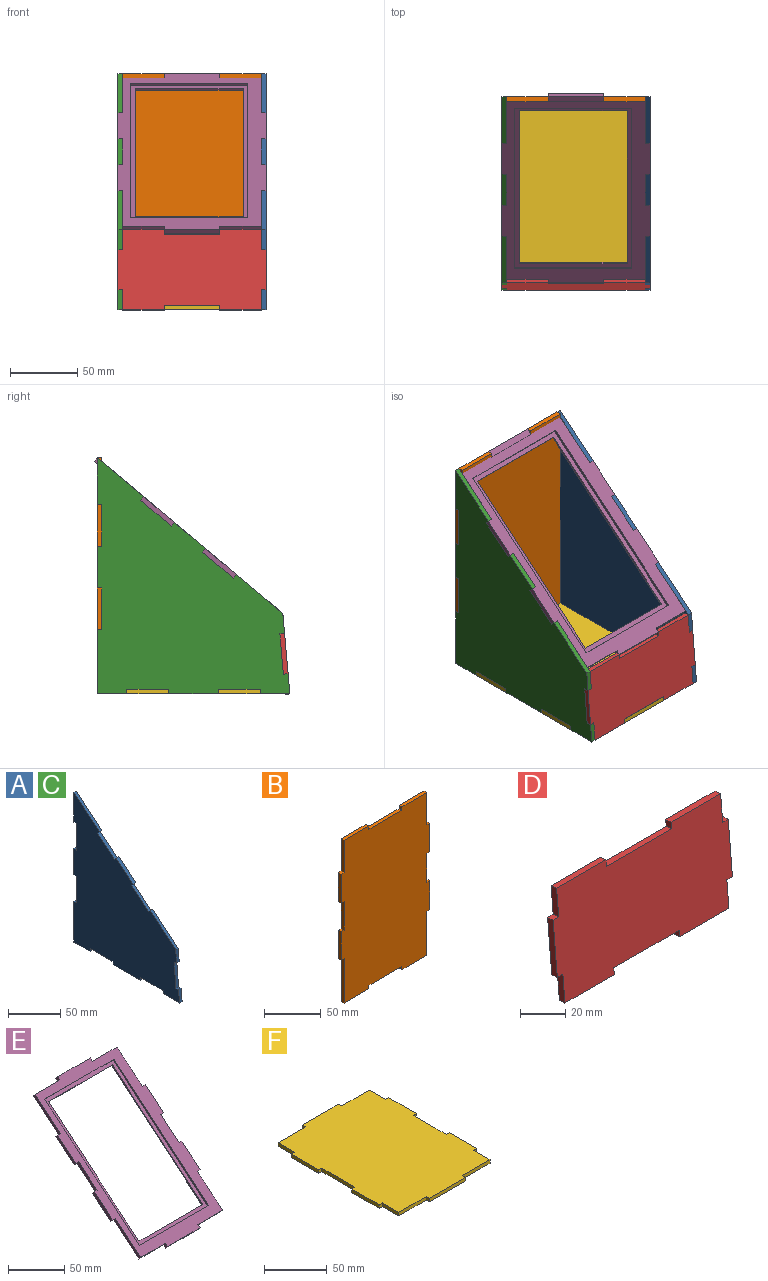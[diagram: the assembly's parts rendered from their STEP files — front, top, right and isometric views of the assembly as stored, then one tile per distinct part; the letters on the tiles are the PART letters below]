
ASSEMBLY  parts=6 mates=5
PART A: 34 faces, bbox 3.5x143.1x175.5 mm
  f0: plane 22.98x19.28mm, normal (0,-0.64,0.77), area 105mm2, adj f1,f31,f32,f33
  f1: plane 3.5x2.68mm, normal (0,0.77,0.64), area 12.2mm2, adj f0,f2,f32,f33
  f2: plane 34.47x28.93mm, normal (0,-0.64,0.77), area 157.5mm2, adj f1,f3,f32,f33
  f3: plane 14.94x3.5mm, normal (0,-1,0.09), area 52.5mm2, adj f2,f4,f32,f33
  f4: plane 3.5x3.49mm, normal (0,-0.09,-1), area 12.2mm2, adj f3,f5,f32,f33
  f5: plane 29.89x3.5mm, normal (0,-1,0.09), area 105mm2, adj f4,f6,f32,f33
  f6: plane 3.5x3.49mm, normal (0,0.09,1), area 12.3mm2, adj f5,f7,f32,f33
  f7: plane 14.94x3.5mm, normal (0,-1,0.09), area 52.5mm2, adj f6,f8,f32,f33
  f8: plane 22x3.5mm, normal (0,0,-1), area 77mm2, adj f7,f9,f32,f33
  f9: plane 3.5x3.5mm, normal (0,1,0), area 12.2mm2, adj f8,f10,f32,f33
  f10: plane 31x3.5mm, normal (0,0,-1), area 108.5mm2, adj f9,f11,f32,f33
  f11: plane 3.5x3.5mm, normal (0,-1,0), area 12.2mm2, adj f10,f12,f32,f33
  f12: plane 37.12x3.5mm, normal (0,0,-1), area 129.9mm2, adj f11,f13,f32,f33
  f13: plane 3.5x3.5mm, normal (0,1,0), area 12.2mm2, adj f12,f14,f32,f33
  f14: plane 31x3.5mm, normal (0,0,-1), area 108.5mm2, adj f13,f15,f32,f33
  f15: plane 3.5x3.5mm, normal (0,-1,0), area 12.2mm2, adj f14,f16,f32,f33
  f16: plane 22x3.5mm, normal (0,0,-1), area 77mm2, adj f15,f17,f32,f33
  f17: plane 47.67x3.5mm, normal (0,1,0), area 166.9mm2, adj f16,f18,f32,f33
  f18: plane 3.5x3.5mm, normal (0,0,1), area 12.3mm2, adj f17,f19,f32,f33
  f19: plane 31x3.5mm, normal (0,1,0), area 108.5mm2, adj f18,f20,f32,f33
  f20: plane 3.5x3.5mm, normal (0,0,-1), area 12.3mm2, adj f19,f21,f32,f33
  f21: plane 31x3.5mm, normal (0,1,0), area 108.5mm2, adj f20,f22,f32,f33
  f22: plane 3.5x3.5mm, normal (0,0,1), area 12.3mm2, adj f21,f23,f32,f33
  f23: plane 31x3.5mm, normal (0,1,0), area 108.5mm2, adj f22,f24,f32,f33
  f24: plane 3.5x3.5mm, normal (0,0,-1), area 12.3mm2, adj f23,f25,f32,f33
  f25: plane 34.8x3.5mm, normal (0,1,0), area 121.8mm2, adj f24,f26,f32,f33
  f26: plane 34.47x28.93mm, normal (0,-0.64,0.77), area 157.5mm2, adj f25,f27,f32,f33
  f27: plane 3.5x2.68mm, normal (0,-0.77,-0.64), area 12.2mm2, adj f26,f28,f32,f33
  f28: plane 22.98x19.28mm, normal (0,-0.64,0.77), area 105mm2, adj f27,f29,f32,f33
  f29: plane 3.5x2.68mm, normal (0,0.77,0.64), area 12.3mm2, adj f28,f30,f32,f33
  f30: plane 22.98x19.28mm, normal (0,-0.64,0.77), area 105mm2, adj f29,f31,f32,f33
  f31: plane 3.5x2.68mm, normal (0,-0.77,-0.64), area 12.3mm2, adj f0,f30,f32,f33
  f32: plane 175.47x143.12mm, normal (1,0,0), area 15626mm2, adj f0,f1,f2,f3,f4,f5,f6,f7
  f33: plane 175.47x143.12mm, normal (-1,0,0), area 15626mm2, adj f0,f1,f2,f3,f4,f5,f6,f7
PART B: 30 faces, bbox 110x3.5x175.5 mm
  f0: plane 3.5x3.5mm, normal (0,0,1), area 12.3mm2, adj f1,f27,f28,f29
  f1: plane 31x3.5mm, normal (1,0,0), area 108.5mm2, adj f0,f2,f28,f29
  f2: plane 3.5x3.5mm, normal (0,0,-1), area 12.3mm2, adj f1,f3,f28,f29
  f3: plane 31x3.5mm, normal (1,0,0), area 108.5mm2, adj f2,f4,f28,f29
  f4: plane 3.5x3.5mm, normal (0,0,1), area 12.3mm2, adj f3,f5,f28,f29
  f5: plane 31x3.5mm, normal (1,0,0), area 108.5mm2, adj f4,f6,f28,f29
  f6: plane 3.5x3.5mm, normal (0,0,-1), area 12.3mm2, adj f5,f7,f28,f29
  f7: plane 47.67x3.5mm, normal (1,0,0), area 166.9mm2, adj f6,f8,f28,f29
  f8: plane 31x3.5mm, normal (0,0,-1), area 108.5mm2, adj f7,f9,f28,f29
  f9: plane 3.5x3.5mm, normal (-1,0,0), area 12.2mm2, adj f8,f10,f28,f29
  f10: plane 41x3.5mm, normal (0,0,-1), area 143.5mm2, adj f9,f11,f28,f29
  f11: plane 3.5x3.5mm, normal (1,0,0), area 12.2mm2, adj f10,f12,f28,f29
  f12: plane 31x3.5mm, normal (0,0,-1), area 108.5mm2, adj f11,f13,f28,f29
  f13: plane 47.67x3.5mm, normal (-1,0,0), area 166.9mm2, adj f12,f14,f28,f29
  f14: plane 3.5x3.5mm, normal (0,0,-1), area 12.3mm2, adj f13,f15,f28,f29
  f15: plane 31x3.5mm, normal (-1,0,0), area 108.5mm2, adj f14,f16,f28,f29
  f16: plane 3.5x3.5mm, normal (0,0,1), area 12.3mm2, adj f15,f17,f28,f29
  f17: plane 31x3.5mm, normal (-1,0,0), area 108.5mm2, adj f16,f18,f28,f29
  f18: plane 3.5x3.5mm, normal (0,0,-1), area 12.3mm2, adj f17,f19,f28,f29
  f19: plane 31x3.5mm, normal (-1,0,0), area 108.5mm2, adj f18,f20,f28,f29
  f20: plane 3.5x3.5mm, normal (0,0,1), area 12.3mm2, adj f19,f21,f28,f29
  f21: plane 34.8x3.5mm, normal (-1,0,0), area 121.8mm2, adj f20,f22,f28,f29
  f22: plane 31x3.5mm, normal (0,0,1), area 108.5mm2, adj f21,f23,f28,f29
  f23: plane 3.5x3.5mm, normal (1,0,0), area 12.3mm2, adj f22,f24,f28,f29
  f24: plane 41x3.5mm, normal (0,0,1), area 143.5mm2, adj f23,f25,f28,f29
  f25: plane 3.5x3.5mm, normal (-1,0,0), area 12.3mm2, adj f24,f26,f28,f29
  f26: plane 31x3.5mm, normal (0,0,1), area 108.5mm2, adj f25,f27,f28,f29
  f27: plane 34.8x3.5mm, normal (1,0,0), area 121.8mm2, adj f0,f26,f28,f29
  f28: plane 175.47x110mm, normal (0,1,0), area 18220.8mm2, adj f0,f1,f2,f3,f4,f5,f6,f7
  f29: plane 175.47x110mm, normal (0,-1,0), area 18220.8mm2, adj f0,f1,f2,f3,f4,f5,f6,f7
PART C: same geometry as A
PART D: 27 faces, bbox 110x8.7x60.1 mm
  f0: plane 110x59.77mm, normal (0,1,-0.09), area 4303mm2, adj f1,f2,f3,f4,f5,f6,f7,f8
  f1: plane 15.25x4.79mm, normal (1,0,0), area 52.5mm2, adj f0,f2,f20,f21
  f2: plane 31x3.49mm, normal (0,0.09,1), area 108.5mm2, adj f0,f1,f3,f21
  f3: plane 3.79x3.79mm, normal (-1,0,0), area 12.3mm2, adj f0,f2,f4,f21
  f4: plane 41x3.49mm, normal (0,0.09,1), area 143.5mm2, adj f0,f3,f5,f21
  f5: plane 3.79x3.79mm, normal (1,0,0), area 12.3mm2, adj f0,f4,f6,f21
  f6: plane 31x3.49mm, normal (0,0.09,1), area 108.5mm2, adj f0,f5,f7,f21
  f7: plane 15.25x4.79mm, normal (-1,0,0), area 52.5mm2, adj f0,f6,f8,f21
  f8: plane 3.5x3.49mm, normal (0,0.09,1), area 12.3mm2, adj f0,f7,f9,f21
  f9: plane 30.19x6.1mm, normal (-1,0,0), area 105mm2, adj f0,f8,f10,f21
  f10: plane 3.5x3.49mm, normal (0,-0.09,-1), area 12.2mm2, adj f0,f9,f11,f21
  f11: plane 15.25x4.79mm, normal (-1,0,0), area 52.5mm2, adj f0,f10,f12,f21
  f12: plane 31x3.49mm, normal (0,-0.09,-1), area 108.5mm2, adj f0,f11,f13,f21
  f13: plane 3.79x3.79mm, normal (1,0,0), area 12.3mm2, adj f0,f12,f14,f21
  f14: plane 41x3.49mm, normal (0,-0.09,-1), area 143.5mm2, adj f0,f13,f15,f21
  f15: plane 3.79x3.79mm, normal (-1,0,0), area 12.3mm2, adj f0,f14,f16,f21
  f16: plane 31x3.49mm, normal (0,-0.09,-1), area 108.5mm2, adj f0,f15,f17,f21
  f17: plane 15.25x4.79mm, normal (1,0,0), area 52.5mm2, adj f0,f16,f18,f21
  f18: plane 3.5x3.49mm, normal (0,-0.09,-1), area 12.2mm2, adj f0,f17,f19,f21
  f19: plane 30.19x6.1mm, normal (1,0,0), area 105mm2, adj f0,f18,f20,f21
  f20: plane 3.5x3.49mm, normal (0,0.09,1), area 12.3mm2, adj f0,f1,f19,f21
  f21: plane 110x59.77mm, normal (0,-1,0.09), area 6103mm2, adj f1,f2,f3,f4,f5,f6,f7,f8
  f22: plane 45x2.49mm, normal (0,-0.09,-1), area 112.5mm2, adj f0,f23,f25,f26
  f23: plane 40.07x5.98mm, normal (-1,0,0), area 100mm2, adj f0,f22,f24,f26
  f24: plane 45x2.49mm, normal (0,0.09,1), area 112.5mm2, adj f0,f23,f25,f26
  f25: plane 40.07x5.98mm, normal (1,0,0), area 100mm2, adj f0,f22,f24,f26
  f26: plane 45x39.85mm, normal (0,1,-0.09), area 1800mm2, adj f22,f23,f24,f25
PART E: 39 faces, bbox 110x140.1x118.4 mm
  f0: plane 120.02x101.16mm, normal (1,0,0), area 310mm2, adj f1,f31,f32,f38
  f1: plane 87x1.53mm, normal (0,-0.77,-0.64), area 174mm2, adj f0,f2,f32,f38
  f2: plane 120.02x101.16mm, normal (-1,0,0), area 310mm2, adj f1,f31,f32,f38
  f3: plane 31x2.68mm, normal (0,0.77,0.64), area 108.5mm2, adj f4,f30,f32,f33
  f4: plane 4.93x4.93mm, normal (1,0,0), area 12.3mm2, adj f3,f5,f32,f33
  f5: plane 41x2.68mm, normal (0,0.77,0.64), area 143.5mm2, adj f4,f6,f32,f33
  f6: plane 4.93x4.93mm, normal (-1,0,0), area 12.2mm2, adj f5,f7,f32,f33
  f7: plane 31x2.68mm, normal (0,0.77,0.64), area 108.5mm2, adj f6,f8,f32,f33
  f8: plane 34.04x29.36mm, normal (-1,0,0), area 145.3mm2, adj f7,f9,f32,f33
  f9: plane 3.5x2.68mm, normal (0,0.77,0.64), area 12.3mm2, adj f8,f10,f32,f33
  f10: plane 25.23x21.96mm, normal (-1,0,0), area 105mm2, adj f9,f11,f32,f33
  f11: plane 3.5x2.68mm, normal (0,-0.77,-0.64), area 12.2mm2, adj f10,f12,f32,f33
  f12: plane 25.23x21.96mm, normal (-1,0,0), area 105mm2, adj f11,f13,f32,f33
  f13: plane 3.5x2.68mm, normal (0,0.77,0.64), area 12.2mm2, adj f12,f14,f32,f33
  f14: plane 25.23x21.96mm, normal (-1,0,0), area 105mm2, adj f13,f15,f32,f33
  f15: plane 3.5x2.68mm, normal (0,-0.77,-0.64), area 12.3mm2, adj f14,f16,f32,f33
  f16: plane 34.04x29.36mm, normal (-1,0,0), area 145.3mm2, adj f15,f17,f32,f33
  f17: plane 31x2.68mm, normal (0,-0.77,-0.64), area 108.5mm2, adj f16,f18,f32,f33
  f18: plane 4.93x4.93mm, normal (-1,0,0), area 12.3mm2, adj f17,f19,f32,f33
  f19: plane 41x2.68mm, normal (0,-0.77,-0.64), area 143.5mm2, adj f18,f20,f32,f33
  f20: plane 4.93x4.93mm, normal (1,0,0), area 12.3mm2, adj f19,f21,f32,f33
  f21: plane 31x2.68mm, normal (0,-0.77,-0.64), area 108.5mm2, adj f20,f22,f32,f33
  f22: plane 34.04x29.36mm, normal (1,0,0), area 145.3mm2, adj f21,f23,f32,f33
  f23: plane 3.5x2.68mm, normal (0,-0.77,-0.64), area 12.3mm2, adj f22,f24,f32,f33
  f24: plane 25.23x21.96mm, normal (1,0,0), area 105mm2, adj f23,f25,f32,f33
  f25: plane 3.5x2.68mm, normal (0,0.77,0.64), area 12.2mm2, adj f24,f26,f32,f33
  f26: plane 25.23x21.96mm, normal (1,0,0), area 105mm2, adj f25,f27,f32,f33
  f27: plane 3.5x2.68mm, normal (0,-0.77,-0.64), area 12.2mm2, adj f26,f28,f32,f33
  f28: plane 25.23x21.96mm, normal (1,0,0), area 105mm2, adj f27,f29,f32,f33
  f29: plane 3.5x2.68mm, normal (0,0.77,0.64), area 12.3mm2, adj f28,f30,f32,f33
  f30: plane 34.04x29.36mm, normal (1,0,0), area 145.3mm2, adj f3,f29,f32,f33
  f31: plane 87x1.53mm, normal (0,0.77,0.64), area 174mm2, adj f0,f2,f32,f38
  f32: plane 137.89x115.7mm, normal (0,-0.64,0.77), area 5041mm2, adj f0,f1,f2,f3,f4,f5,f6,f7
  f33: plane 137.89x115.7mm, normal (0,0.64,-0.77), area 6686mm2, adj f3,f4,f5,f6,f7,f8,f9,f10
  f34: plane 114.34x96.28mm, normal (1,0,0), area 222mm2, adj f33,f35,f37,f38
  f35: plane 80x1.15mm, normal (0,-0.77,-0.64), area 120mm2, adj f33,f34,f36,f38
  f36: plane 114.34x96.28mm, normal (-1,0,0), area 222mm2, adj f33,f35,f37,f38
  f37: plane 80x1.15mm, normal (0,0.77,0.64), area 120mm2, adj f33,f34,f36,f38
  f38: plane 118.74x99.63mm, normal (0,-0.64,0.77), area 1645mm2, adj f0,f1,f2,f31,f34,f35,f36,f37
PART F: 30 faces, bbox 110x143.1x3.5 mm
  f0: plane 31x3.5mm, normal (0,1,0), area 108.5mm2, adj f1,f27,f28,f29
  f1: plane 18.5x3.5mm, normal (1,0,0), area 64.8mm2, adj f0,f2,f28,f29
  f2: plane 3.5x3.5mm, normal (0,1,0), area 12.3mm2, adj f1,f3,f28,f29
  f3: plane 31x3.5mm, normal (1,0,0), area 108.5mm2, adj f2,f4,f28,f29
  f4: plane 3.5x3.5mm, normal (0,-1,0), area 12.3mm2, adj f3,f5,f28,f29
  f5: plane 37.12x3.5mm, normal (1,0,0), area 129.9mm2, adj f4,f6,f28,f29
  f6: plane 3.5x3.5mm, normal (0,1,0), area 12.3mm2, adj f5,f7,f28,f29
  f7: plane 31x3.5mm, normal (1,0,0), area 108.5mm2, adj f6,f8,f28,f29
  f8: plane 3.5x3.5mm, normal (0,-1,0), area 12.2mm2, adj f7,f9,f28,f29
  f9: plane 18.5x3.5mm, normal (1,0,0), area 64.8mm2, adj f8,f10,f28,f29
  f10: plane 31x3.5mm, normal (0,-1,0), area 108.5mm2, adj f9,f11,f28,f29
  f11: plane 3.5x3.5mm, normal (1,0,0), area 12.2mm2, adj f10,f12,f28,f29
  f12: plane 41x3.5mm, normal (0,-1,0), area 143.5mm2, adj f11,f13,f28,f29
  f13: plane 3.5x3.5mm, normal (-1,0,0), area 12.2mm2, adj f12,f14,f28,f29
  f14: plane 31x3.5mm, normal (0,-1,0), area 108.5mm2, adj f13,f15,f28,f29
  f15: plane 18.5x3.5mm, normal (-1,0,0), area 64.8mm2, adj f14,f16,f28,f29
  f16: plane 3.5x3.5mm, normal (0,-1,0), area 12.3mm2, adj f15,f17,f28,f29
  f17: plane 31x3.5mm, normal (-1,0,0), area 108.5mm2, adj f16,f18,f28,f29
  f18: plane 3.5x3.5mm, normal (0,1,0), area 12.3mm2, adj f17,f19,f28,f29
  f19: plane 37.12x3.5mm, normal (-1,0,0), area 129.9mm2, adj f18,f20,f28,f29
  f20: plane 3.5x3.5mm, normal (0,-1,0), area 12.3mm2, adj f19,f21,f28,f29
  f21: plane 31x3.5mm, normal (-1,0,0), area 108.5mm2, adj f20,f22,f28,f29
  f22: plane 3.5x3.5mm, normal (0,1,0), area 12.3mm2, adj f21,f23,f28,f29
  f23: plane 18.5x3.5mm, normal (-1,0,0), area 64.8mm2, adj f22,f24,f28,f29
  f24: plane 31x3.5mm, normal (0,1,0), area 108.5mm2, adj f23,f25,f28,f29
  f25: plane 3.5x3.5mm, normal (-1,0,0), area 12.3mm2, adj f24,f26,f28,f29
  f26: plane 41x3.5mm, normal (0,1,0), area 143.5mm2, adj f25,f27,f28,f29
  f27: plane 3.5x3.5mm, normal (1,0,0), area 12.3mm2, adj f0,f26,f28,f29
  f28: plane 143.12x110mm, normal (0,0,-1), area 14741.1mm2, adj f0,f1,f2,f3,f4,f5,f6,f7
  f29: plane 143.12x110mm, normal (0,0,1), area 14741.1mm2, adj f0,f1,f2,f3,f4,f5,f6,f7
PLACE A t=(-15.93,-4.39,0.9)mm
PLACE B t=(-15.93,-7.89,0.9)mm
PLACE C t=(-122.43,-4.39,0.9)mm
PLACE D t=(-15.93,-0.91,0.6)mm fixed
PLACE E t=(-15.93,-2.14,-1.78)mm
PLACE F t=(-15.93,7.43,4.4)mm
MATE fastened C.f33 <-> F.f17  axis (-1,0,0) through (-122.43,-38.23,-55.97)mm
MATE fastened A.f25 <-> B.f28  axis (0,1,0) through (-15.93,82.89,81.21)mm
MATE fastened F.f28 <-> A.f8  axis (0,0,1) through (-15.93,-38.23,-59.47)mm
MATE fastened D.f19 <-> A.f32  axis (1,0,0) through (-12.43,-52.82,-14.94)mm
MATE fastened E.f32 <-> A.f30  axis (0,-0.64,0.77) through (-12.43,2.46,48.51)mm
